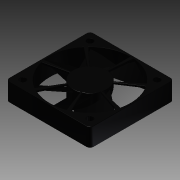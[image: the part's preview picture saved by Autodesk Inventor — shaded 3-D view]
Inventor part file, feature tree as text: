
AUTODESK INVENTOR PART (.ipt)
format: ipt  version: 2015 (Build 190159000, 159)  size: 420,352 bytes
history: native  units: in
note: dims shown in document units (in); Inventor stores cm internally (conversion verified against a paired STEP export)
features: sketch x5, extrude x3, plane x1, pattern_circular x1, fillet x1, projected_geometry x1
ambient origin geometry x8: Origin, YZ Plane, XZ Plane, XY Plane, X Axis, Y Axis, Z Axis, Center Point
bodies: Solid1 (feature_tree)
feature tree (12):
  extrude  "Extrusion2"  Depth=1.9685in
  extrude  "Extrusion3"  Depth=1.5748in
  sketch  "Sketch4"  dims[d8=0.1378in d9=0.0787in]
  plane  "Work Plane1"
  extrude  "Extrusion4"  Depth=0.0787in
  sketch  "Sketch6"  dims[d11=1.8898in d12=0.4213in d13=0.0in d14=0.0787in d15=0.0787in d16=0.7874in d22=0.0394in d23=0.0in d25=0.0344in d30=2.7559in d32=360.0deg d37=60.0deg d38=0.0157in d41=0.0079in d43=0.937in d44=0.0in d45=0.0079in d46=0.2716in d48=2.7559in d49=360.0deg d51=0.0079in]
  pattern_circular  "Circular Pattern1"  [2 undecoded]
  fillet  "Fillet1"  Radius=0.0787in
  sketch  "Sketch2"  dims[d4=1.9685in d5=1.9685in]
  sketch  "Sketch3"  dims[d6=1.5748in d7=1.5748in]
  sketch  "Sketch5"  dims[d10=0.0787in]
  projected_geometry  "Projected Loop1"
note: 2 required parameter values undecoded (feature->parameter linkage not recoverable at this tier; creation-order binding heuristic only, values carry confidence <= 0.55)
